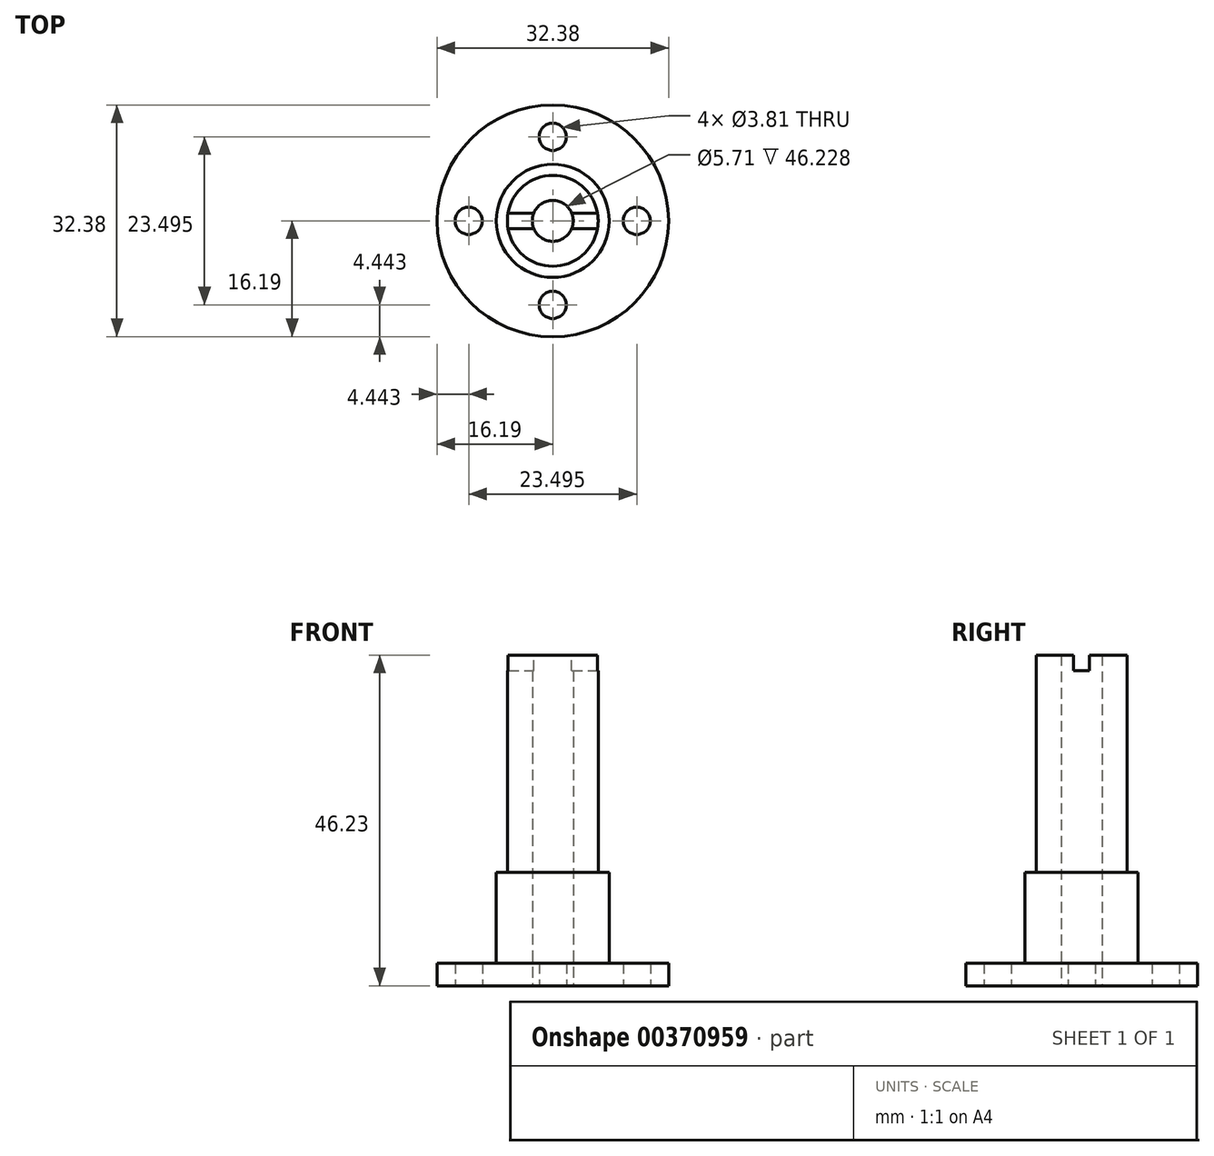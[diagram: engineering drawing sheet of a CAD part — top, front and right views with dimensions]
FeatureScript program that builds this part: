
annotation { "Feature Type Name" : "Feature", "Feature Type Description" : "" }
export const myFeature = defineFeature(function(context is Context, id is Id, definition is map)
    precondition{}
    {
        {
            var Q0;
            Q0=qCreatedBy(makeId("Top.planeOp"),FACE);
            var sketch = newSketch(context, id + "F0", { "sketchPlane" : qUnion([Q0])});
            skCircle(sketch, "E0", {"center": v(0, 0) * mm, "radius": 2.86 * mm});
            skCircle(sketch, "E1", {"center": v(0, 0) * mm, "radius": 6.35 * mm});
            skCircle(sketch, "E2", {"center": v(0, 0) * mm, "radius": 16.2 * mm});
            skCircle(sketch, "E3", {"center": v(0, 0) * mm, "radius": 11.75 * mm, "construction": true});
            skLineSegment(sketch, "E4", {"start": v(0, 0) * mm, "end": v(0, 12.88) * mm, "construction": true});
            skLineSegment(sketch, "E5", {"start": v(0, 0) * mm, "end": v(13.44, 0) * mm, "construction": true});
            skLineSegment(sketch, "E6", {"start": v(0, 0) * mm, "end": v(0, -11.5) * mm, "construction": true});
            skLineSegment(sketch, "E7", {"start": v(0, 0) * mm, "end": v(-13.18, 0) * mm, "construction": true});
            skCircle(sketch, "E8", {"center": v(-11.75, 0) * mm, "radius": 1.9 * mm});
            skCircle(sketch, "E9", {"center": v(11.75, 0) * mm, "radius": 1.9 * mm});
            skCircle(sketch, "E10", {"center": v(0, -11.75) * mm, "radius": 1.9 * mm});
            skCircle(sketch, "E11", {"center": v(0, 11.75) * mm, "radius": 1.9 * mm});
            skCircle(sketch, "E12", {"center": v(0, 0) * mm, "radius": 7.9 * mm});
            skSolve(sketch);
        }
        {
            var Q0;
            Q0=makeQuery(id+"F0.imprint","IMPRINT",FACE,{"disambiguationData":[TD([[makeQuery(id+"F0.imprint","IMPRINT",EDGE,{"derivedFrom":sQuery(id+"F0.wireOp",EDGE,"E1")}),-1.0]])]});
            extrude(context, id + "F1", {"entities" : qUnion([Q0]), "depth" : 15.88 * mm});
        }
        {
            var Q0;
            Q0=makeQuery(id+"F0.imprint","IMPRINT",FACE,{"disambiguationData":[TD([[makeQuery(id+"F0.imprint","IMPRINT",EDGE,{"derivedFrom":sQuery(id+"F0.wireOp",EDGE,"E0")}),-1.0]])]});
            extrude(context, id + "F2", {"entities" : qUnion([Q0]), "operationType" : NewBodyOperationType.ADD, "offsetDistance" : 25.4 * mm, "depth" : 46.23 * mm});
        }
        {
            var Q0;
            Q0=makeQuery(id+"F2.opExtrude","CAP_FACE",FACE,{"disambiguationData":[OSD([sQuery(id+"F0.wireOp",EDGE,"E0"),sQuery(id+"F0.wireOp",EDGE,"E1")])],"isStart":false});
            var sketch = newSketch(context, id + "F3", { "sketchPlane" : qUnion([Q0])});
            skPoint(sketch, "E13", {"position": v(0.93, 6.28) * mm});
            skSolve(sketch);
        }
        {
            var Q0;
            Q0=makeQuery(id+"F0.imprint","IMPRINT",FACE,{"disambiguationData":[TD([[makeQuery(id+"F0.imprint","IMPRINT",EDGE,{"derivedFrom":sQuery(id+"F0.wireOp",EDGE,"E2")}),1.0]])]});
            extrude(context, id + "F4", {"entities" : qUnion([Q0]), "operationType" : NewBodyOperationType.ADD, "offsetDistance" : 25.4 * mm, "depth" : 3.17 * mm});
        }
        {
            var Q0;
            Q0=makeQuery(id+"F3.imprint","IMPRINT",FACE,{"disambiguationData":[TD([[makeQuery(id+"F3.imprint","IMPRINT",EDGE,{"derivedFrom":makeQuery(id+"F2.opExtrude","CAP_EDGE",EDGE,{"disambiguationData":[OSD([sQuery(id+"F0.wireOp",EDGE,"E0")])],"isStart":false})}),-1.0]])]});
            var sketch = newSketch(context, id + "F5", { "sketchPlane" : qUnion([Q0])});
            skLineSegment(sketch, "E14.bottom", {"start": v(-6.25, 1.1) * mm, "end": v(6.25, 1.1) * mm});
            skLineSegment(sketch, "E14.top", {"start": v(-6.25, -1.1) * mm, "end": v(6.25, -1.1) * mm});
            skPoint(sketch, "E14.middle", {"position": v(0, 0) * mm});
            skSolve(sketch);
        }
        {
            var Q0;
            {var subQ0=sQuery(id+"F5.wireOp",EDGE,"E14.bottom");var subQ1=makeQuery(id+"F3.imprint","IMPRINT",EDGE,{"derivedFrom":makeQuery(id+"F2.opExtrude","CAP_EDGE",EDGE,{"disambiguationData":[OSD([sQuery(id+"F0.wireOp",EDGE,"E1")])],"isStart":false})});var subQ2=makeQuery(id+"F5.imprint","INTERSECT",VERTEX,{"disambiguationData":[OD(0.0)],"derivedFrom":[subQ1,subQ0]});Q0=makeQuery(id+"F5.imprint","IMPRINT",FACE,{"disambiguationData":[TD([[makeQuery(id+"F5.imprint","IMPRINT",EDGE,{"disambiguationData":[TD([[subQ2,-1.0]])],"derivedFrom":subQ0}),-1.0]])]});}
            var Q1;
            {var subQ0=sQuery(id+"F5.wireOp",EDGE,"E14.bottom");var subQ1=makeQuery(id+"F3.imprint","IMPRINT",EDGE,{"derivedFrom":makeQuery(id+"F2.opExtrude","CAP_EDGE",EDGE,{"disambiguationData":[OSD([sQuery(id+"F0.wireOp",EDGE,"E1")])],"isStart":false})});var subQ2=makeQuery(id+"F5.imprint","INTERSECT",VERTEX,{"disambiguationData":[OD(1.0)],"derivedFrom":[subQ1,subQ0]});Q1=makeQuery(id+"F5.imprint","IMPRINT",FACE,{"disambiguationData":[TD([[makeQuery(id+"F5.imprint","IMPRINT",EDGE,{"disambiguationData":[TD([[subQ2,1.0]])],"derivedFrom":subQ0}),-1.0]])]});}
            extrude(context, id + "F6", {"entities" : qUnion([Q0, Q1]), "operationType" : NewBodyOperationType.REMOVE, "flatOperationType" : FlatOperationType.REMOVE, "thickness1" : 5 * mm, "thickness2" : 0 * mm, "oppositeDirection" : true, "offsetDistance" : 25 * mm, "startOffsetBound" : StartOffsetType.BLIND, "startOffsetDistance" : 25 * mm, "depth" : 2.2 * mm, "domain" : OperationDomain.MODEL});
        }
    });
